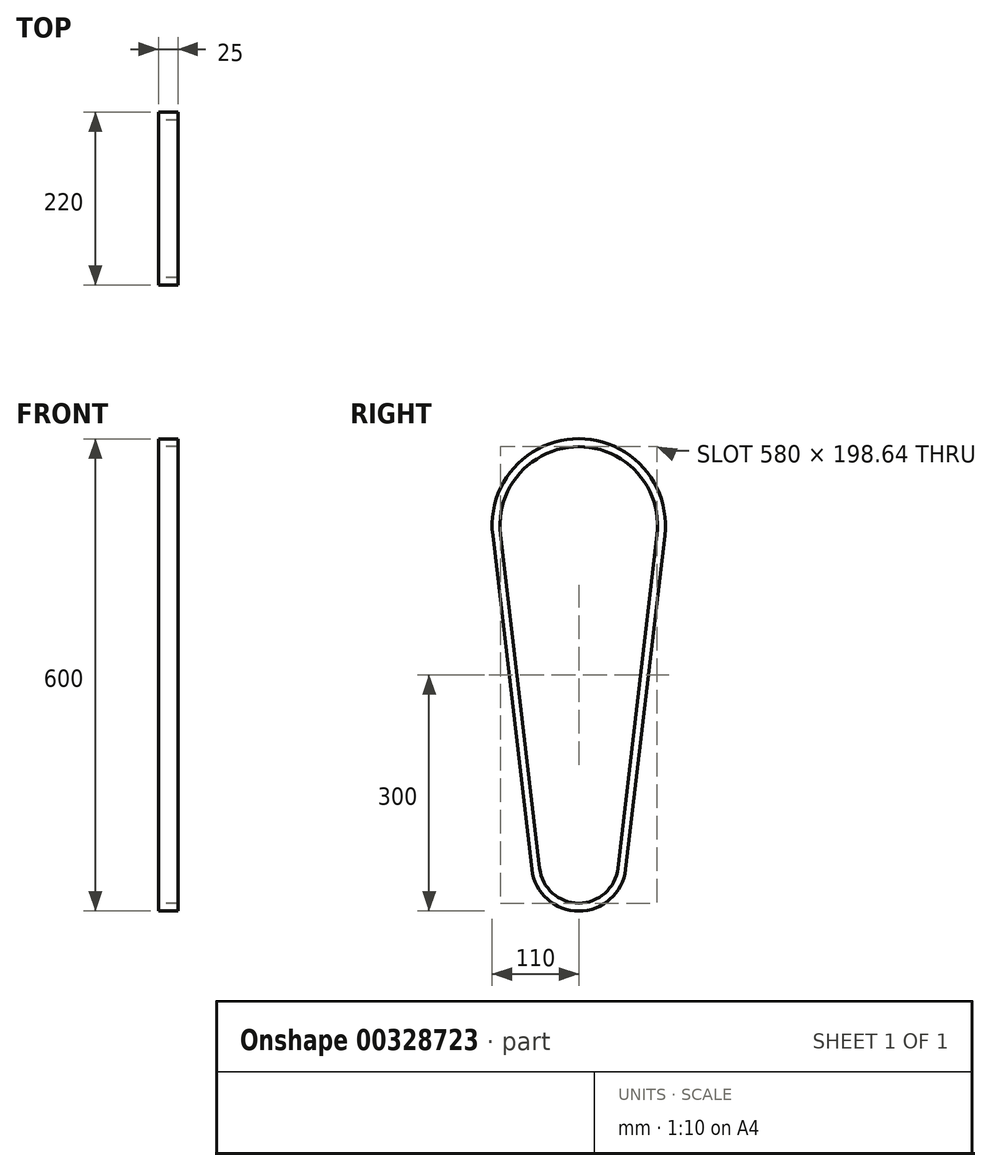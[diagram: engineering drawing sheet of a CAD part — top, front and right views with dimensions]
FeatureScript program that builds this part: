
annotation { "Feature Type Name" : "Feature", "Feature Type Description" : "" }
export const myFeature = defineFeature(function(context is Context, id is Id, definition is map)
    precondition{}
    {
        {
            var Q0;
            Q0=qCreatedBy(makeId("Right.planeOp"),FACE);
            var sketch = newSketch(context, id + "F0", { "sketchPlane" : qUnion([Q0])});
            skArc(sketch, "E0", {"start": v(99.32, -11.63) * mm, "mid": v(0, 100) * mm, "end": v(-99.32, -11.63) * mm});
            skArc(sketch, "E1", {"start": v(-49.66, -435.81) * mm, "mid": v(0, -480) * mm, "end": v(49.66, -435.81) * mm});
            skLineSegment(sketch, "E2", {"start": v(-99.32, -11.63) * mm, "end": v(-49.66, -435.81) * mm});
            skLineSegment(sketch, "E3", {"start": v(99.32, -11.63) * mm, "end": v(49.66, -435.81) * mm});
            skLineSegment(sketch, "E4.0", {"start": v(-109.25, -12.8) * mm, "end": v(-59.6, -436.98) * mm});
            skArc(sketch, "E4.1", {"start": v(109.25, -12.8) * mm, "mid": v(0, 110) * mm, "end": v(-109.25, -12.8) * mm});
            skLineSegment(sketch, "E4.2", {"start": v(109.25, -12.8) * mm, "end": v(59.6, -436.98) * mm});
            skArc(sketch, "E4.3", {"start": v(-59.6, -436.98) * mm, "mid": v(0, -490) * mm, "end": v(59.6, -436.98) * mm});
            skSolve(sketch);
        }
        {
            var Q0;
            Q0 = qSketchRegion(id + "F0", true);
            extrude(context, id + "F1", {"entities" : qUnion([Q0]), "depth" : 25 * mm});
        }
    });
